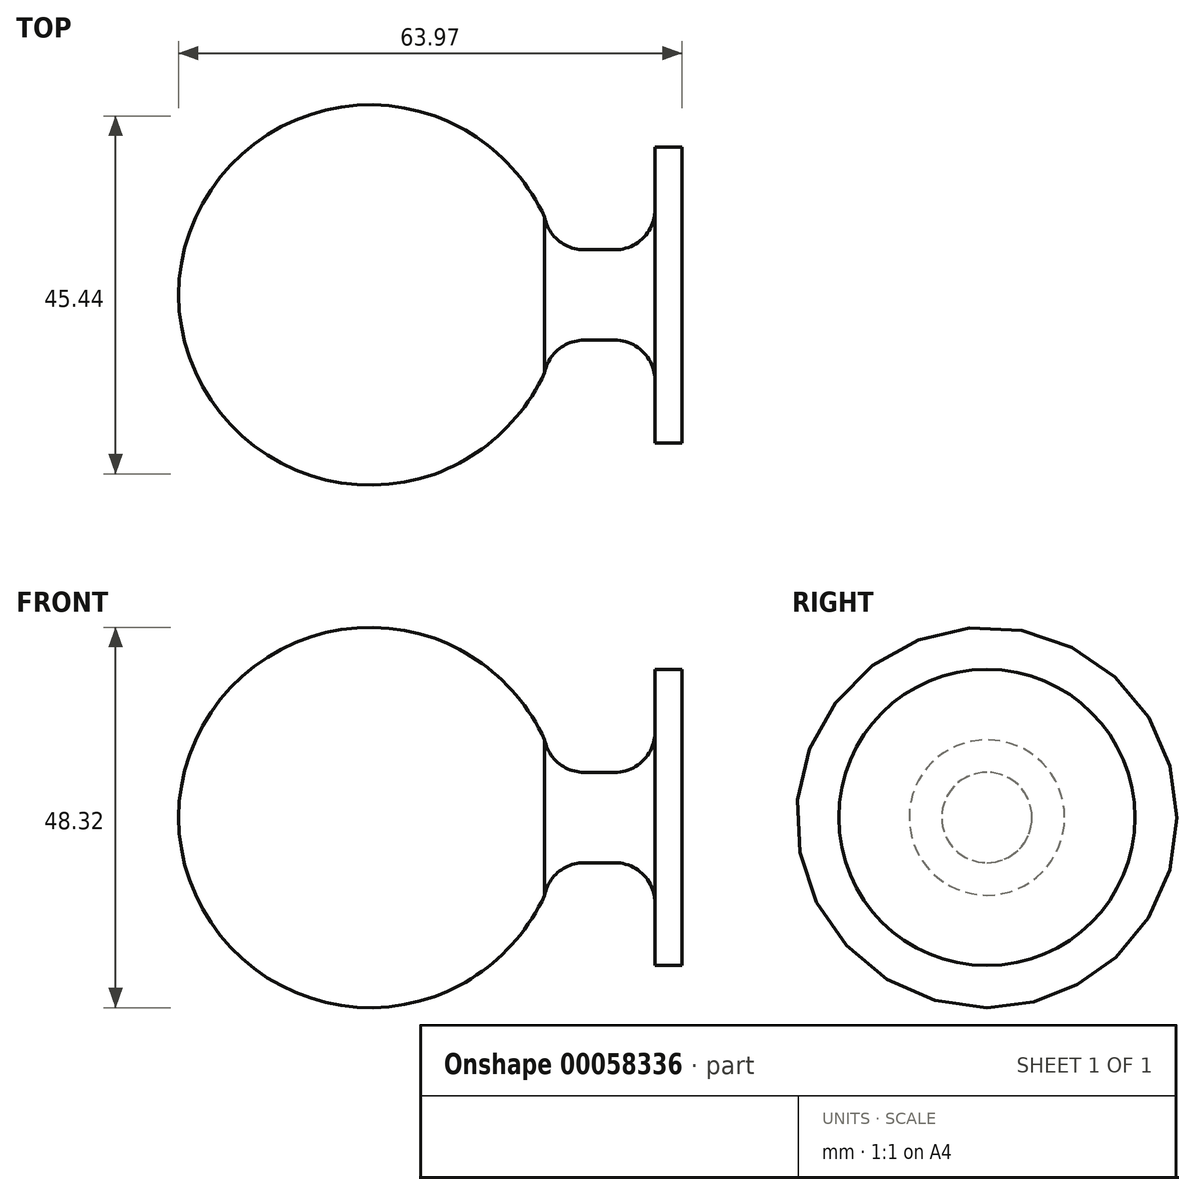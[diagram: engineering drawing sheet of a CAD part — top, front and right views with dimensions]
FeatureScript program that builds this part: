
annotation { "Feature Type Name" : "Feature", "Feature Type Description" : "" }
export const myFeature = defineFeature(function(context is Context, id is Id, definition is map)
    precondition{}
    {
        {
            var Q0;
            Q0=qCreatedBy(makeId("Front.planeOp"),FACE);
            var sketch = newSketch(context, id + "F0", { "sketchPlane" : qUnion([Q0])});
            skArc(sketch, "E0", {"start": v(32.62, 22.72) * mm, "mid": v(10.44, 19.78) * mm, "end": v(0, 0) * mm});
            skArc(sketch, "E1", {"start": v(46.52, 9.87) * mm, "mid": v(40.84, 17.67) * mm, "end": v(32.62, 22.72) * mm});
            skLineSegment(sketch, "E2", {"start": v(60.51, 18.81) * mm, "end": v(60.51, 11.12) * mm});
            skLineSegment(sketch, "E3", {"start": v(46.52, 9.87) * mm, "end": v(46.52, 5.74) * mm});
            skLineSegment(sketch, "E4", {"start": v(46.52, 5.74) * mm, "end": v(60.51, 5.74) * mm});
            skLineSegment(sketch, "E5", {"start": v(0, 0) * mm, "end": v(60.51, 0) * mm});
            skLineSegment(sketch, "E6", {"start": v(63.97, 0) * mm, "end": v(63.97, 18.81) * mm});
            skLineSegment(sketch, "E7", {"start": v(63.97, 18.81) * mm, "end": v(60.51, 18.81) * mm});
            skLineSegment(sketch, "E8", {"start": v(60.51, 0) * mm, "end": v(63.97, 0) * mm});
            skLineSegment(sketch, "E9", {"start": v(60.51, 11.12) * mm, "end": v(60.51, 5.74) * mm});
            skSolve(sketch);
        }
        {
            var Q0;
            Q0=makeQuery(id+"F0.imprint","IMPRINT",FACE,{"disambiguationData":[TD([[makeQuery(id+"F0.imprint","IMPRINT",EDGE,{"derivedFrom":sQuery(id+"F0.wireOp",EDGE,"E0")}),1.0]])]});
            var Q1;
            Q1=sQuery(id+"F0.wireOp",EDGE,"E5");
            revolve(context, id + "F1", {"entities" : qUnion([Q0]), "axis" : qUnion([Q1]), "revolveType" : RevolveType.FULL});
        }
        {
            var Q0;
            Q0=makeQuery(id+"F1.opRevolve","SWEPT_EDGE",EDGE,{"disambiguationData":[OSD([sQuery(id+"F0.wireOp",EDGE,"E3"),sQuery(id+"F0.wireOp",EDGE,"E4")])]});
            var Q1;
            Q1=makeQuery(id+"F1.opRevolve","SWEPT_EDGE",EDGE,{"disambiguationData":[OSD([sQuery(id+"F0.wireOp",EDGE,"E4"),sQuery(id+"F0.wireOp",EDGE,"E9")])]});
            fillet(context, id + "F2", {"entities" : qUnion([Q0, Q1]), "radius" : 5.08 * mm, "tangentPropagation" : true, "allowEdgeOverflow" : false});
        }
    });
